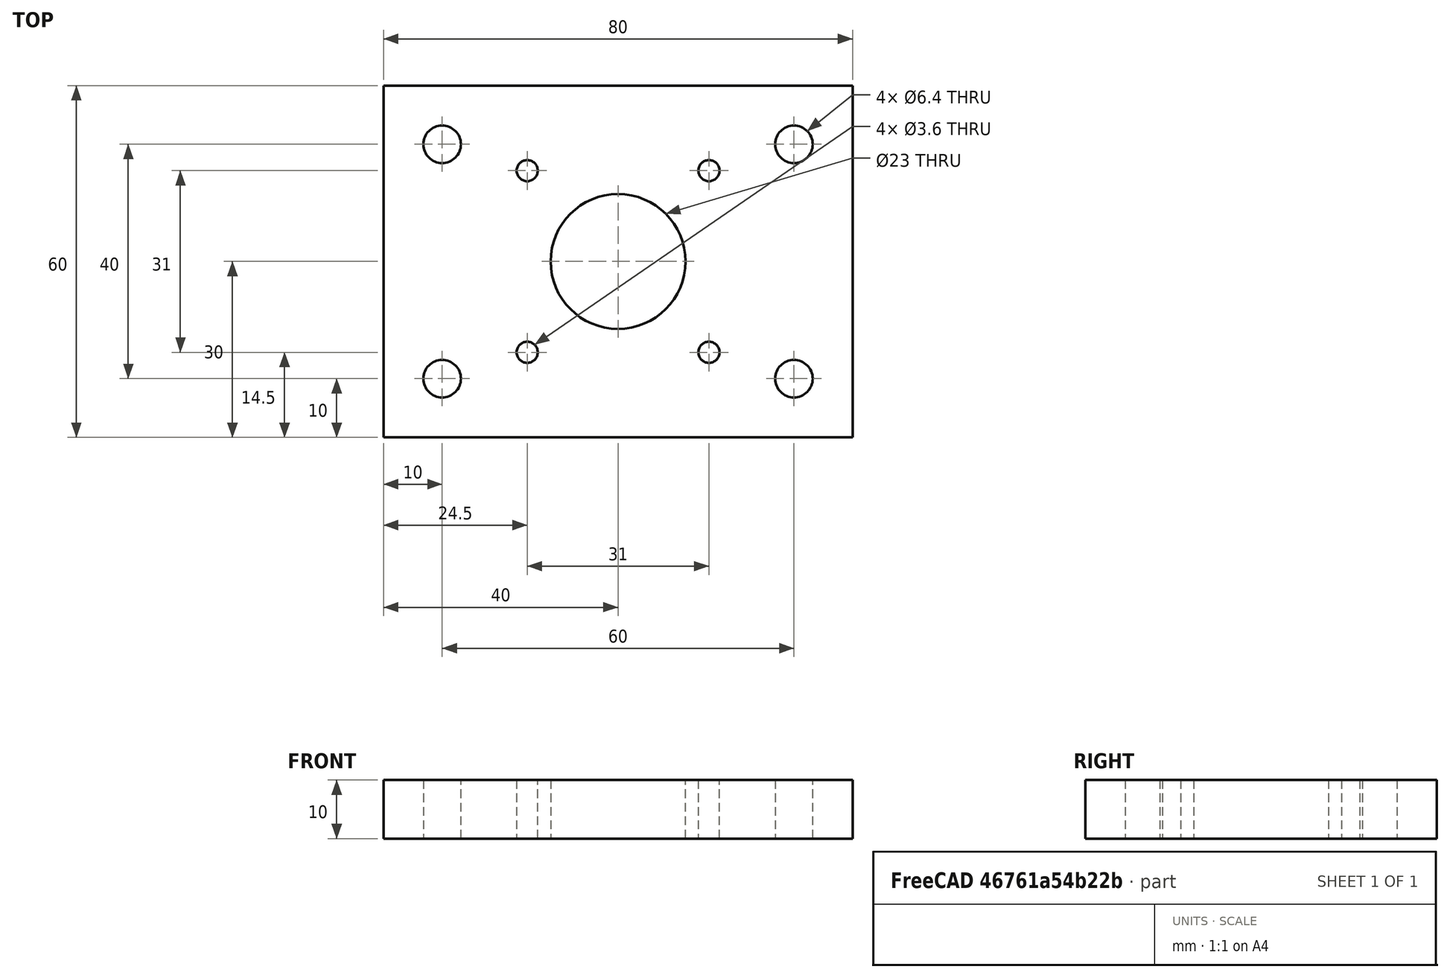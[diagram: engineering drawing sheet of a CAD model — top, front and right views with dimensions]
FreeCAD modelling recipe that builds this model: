
FCSTD DOCUMENT  (FreeCAD 0.18R16110 (Git))
Label: mountplate1c_motor
License: All rights reserved
LicenseURL: http://en.wikipedia.org/wiki/All_rights_reserved
objects: Sketcher::SketchObject×1, PartDesign::Pad×1, PartDesign::Body×1
note: 4 computed .brp shape members not serialized (recipe doc carries the construction recipe); baked Part::Feature solids carry a one-line shape summary decoded from their .brp

FEATURE [Sketcher::SketchObject] Sketch
  MapMode = 5
  Support = -> [XY_Plane]
  sketch-geometry (13):
    g0: LineSegment StartX=0 StartY=60 StartZ=0 EndX=80 EndY=60 EndZ=0
    g1: LineSegment StartX=80 StartY=60 StartZ=0 EndX=80 EndY=0 EndZ=0
    g2: LineSegment StartX=80 StartY=0 StartZ=0 EndX=0 EndY=0 EndZ=0
    g3: LineSegment StartX=0 StartY=0 StartZ=0 EndX=0 EndY=60 EndZ=0
    g4: Circle CenterX=40 CenterY=30 CenterZ=0 NormalX=0 NormalY=0 NormalZ=1 AngleXU=0 Radius=11.5
    g5: Circle CenterX=55.5 CenterY=45.5 CenterZ=0 NormalX=0 NormalY=0 NormalZ=1 AngleXU=0 Radius=1.8
    g6: Circle CenterX=55.5 CenterY=14.5 CenterZ=0 NormalX=0 NormalY=0 NormalZ=1 AngleXU=0 Radius=1.8
    g7: Circle CenterX=24.5 CenterY=14.5 CenterZ=0 NormalX=0 NormalY=0 NormalZ=1 AngleXU=0 Radius=1.8
    g8: Circle CenterX=24.5 CenterY=45.5 CenterZ=0 NormalX=0 NormalY=0 NormalZ=1 AngleXU=0 Radius=1.8
    g9: Circle CenterX=10 CenterY=10 CenterZ=0 NormalX=0 NormalY=0 NormalZ=1 AngleXU=0 Radius=3.2
    g10: Circle CenterX=70 CenterY=10 CenterZ=0 NormalX=0 NormalY=0 NormalZ=1 AngleXU=0 Radius=3.2
    g11: Circle CenterX=10 CenterY=50 CenterZ=0 NormalX=0 NormalY=0 NormalZ=1 AngleXU=0 Radius=3.2
    g12: Circle CenterX=70 CenterY=50 CenterZ=0 NormalX=0 NormalY=0 NormalZ=1 AngleXU=0 Radius=3.2
  constraints (38):
    c: Coincident(g0,g1)
    c: Coincident(g1,g2)
    c: Coincident(g2,g3)
    c: Coincident(g3,g0)
    c: Horizontal(g0)
    c: Horizontal(g2)
    c: Vertical(g1)
    c: Vertical(g3)
    c: Coincident(g2,g-1)
    c: DistanceY(g3,g3) = 60
    c: DistanceX(g2,g2) = 80
    c: DistanceX(g2,g4) = 40
    c: DistanceY(g2,g4) = 30
    c: Radius(g4) = 11.5
    c: DistanceY(g4,g5) = 15.5
    c: DistanceX(g6,g5) = 0
    c: DistanceX(g4,g5) = 15.5
    c: DistanceY(g8,g5) = 0
    c: DistanceX(g8,g5) = 31
    c: DistanceX(g7,g8) = 0
    c: DistanceY(g6,g5) = 31
    c: DistanceY(g6,g7) = 0
    c: Radius(g8) = 1.8
    c: Equal(g8,g5)
    c: Equal(g8,g6)
    c: Equal(g8,g7)
    c: DistanceX(g2,g9) = 10
    c: DistanceY(g2,g9) = 10
    c: DistanceY(g9,g10) = 0
    c: DistanceX(g10,g1) = 10
    c: Radius(g9) = 3.2
    c: Equal(g9,g10)
    c: DistanceY(g11,g0) = 10
    c: DistanceY(g12,g0) = 10
    c: Radius(g12) = 3.2
    c: Radius(g11) = 3.2
    c: DistanceX(g11,g9) = 0
    c: DistanceX(g10,g12) = 0
FEATURE [PartDesign::Pad] Pad
  Length = 10
  Length2 = 100
  Profile = -> Sketch
  Type = 0
FEATURE [PartDesign::Body] Body
  Group = -> [Sketch,Pad]
  Origin = -> Origin
  Tip = -> Pad
